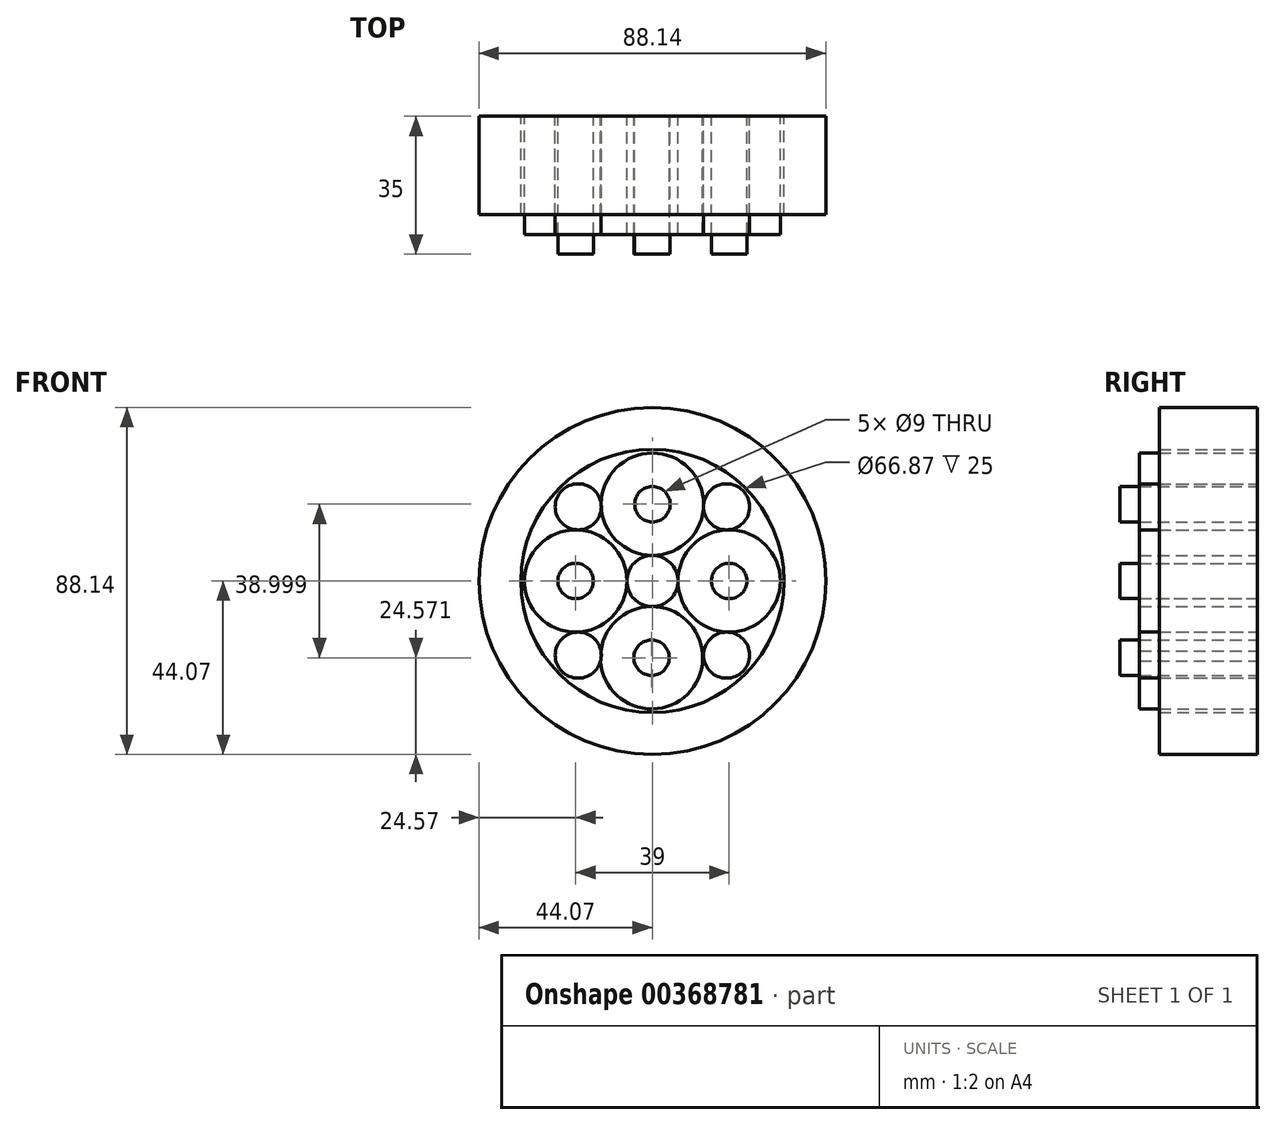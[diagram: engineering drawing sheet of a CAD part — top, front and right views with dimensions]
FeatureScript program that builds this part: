
annotation { "Feature Type Name" : "Feature", "Feature Type Description" : "" }
export const myFeature = defineFeature(function(context is Context, id is Id, definition is map)
    precondition{}
    {
        {
            var Q0;
            Q0=qCreatedBy(makeId("Front.planeOp"),FACE);
            var sketch = newSketch(context, id + "F0", { "sketchPlane" : qUnion([Q0])});
            skCircle(sketch, "E0", {"center": v(0, 0) * mm, "radius": 6.5 * mm});
            skCircle(sketch, "E1", {"center": v(0, 19.5) * mm, "radius": 13 * mm});
            skCircle(sketch, "E2", {"center": v(19.5, 0) * mm, "radius": 13 * mm});
            skCircle(sketch, "E3", {"center": v(-0.21, -19.5) * mm, "radius": 13 * mm});
            skCircle(sketch, "E4", {"center": v(-19.5, 0) * mm, "radius": 13 * mm});
            skCircle(sketch, "E5", {"center": v(0, 0) * mm, "radius": 32.5 * mm});
            skCircle(sketch, "E6", {"center": v(0, 19.5) * mm, "radius": 4.5 * mm});
            skCircle(sketch, "E7", {"center": v(19.5, 0) * mm, "radius": 4.5 * mm});
            skCircle(sketch, "E8", {"center": v(-19.5, 0) * mm, "radius": 4.5 * mm});
            skCircle(sketch, "E9", {"center": v(-0.21, -19.5) * mm, "radius": 4.5 * mm});
            skCircle(sketch, "E10", {"center": v(-18.84, 18.84) * mm, "radius": 5.85 * mm});
            skPoint(sketch, "E10.first.point", {"position": v(-19.05, 13) * mm});
            skPoint(sketch, "E10.second.point", {"position": v(-22.98, 22.98) * mm});
            skPoint(sketch, "E10.third.point", {"position": v(-13, 19.05) * mm});
            skPoint(sketch, "E11.first.point", {"position": v(19.05, 13) * mm});
            skPoint(sketch, "E11.second.point", {"position": v(13, 19.05) * mm});
            skPoint(sketch, "E11.third.point", {"position": v(22.98, 22.98) * mm});
            skCircle(sketch, "E12.1.0", {"center": v(-18.84, -18.84) * mm, "radius": 5.85 * mm});
            skCircle(sketch, "E12.2.0", {"center": v(18.84, -18.84) * mm, "radius": 5.85 * mm});
            skCircle(sketch, "E12.3.0", {"center": v(18.84, 18.84) * mm, "radius": 5.85 * mm});
            skSolve(sketch);
        }
        {
            var Q0;
            Q0=makeQuery(id+"F0.imprint","IMPRINT",FACE,{"disambiguationData":[TD([[makeQuery(id+"F0.imprint","IMPRINT",EDGE,{"derivedFrom":sQuery(id+"F0.wireOp",EDGE,"E6")}),1.0]])]});
            extrude(context, id + "F1", {"entities" : qUnion([Q0]), "depth" : 35 * mm});
        }
        {
            var Q0;
            Q0=makeQuery(id+"F0.imprint","IMPRINT",FACE,{"disambiguationData":[TD([[makeQuery(id+"F0.imprint","IMPRINT",EDGE,{"derivedFrom":sQuery(id+"F0.wireOp",EDGE,"E6")}),-1.0]])]});
            extrude(context, id + "F2", {"entities" : qUnion([Q0]), "depth" : 30 * mm});
        }
        {
            var Q0;
            Q0=makeQuery(id+"F0.imprint","IMPRINT",FACE,{"disambiguationData":[TD([[makeQuery(id+"F0.imprint","IMPRINT",EDGE,{"derivedFrom":sQuery(id+"F0.wireOp",EDGE,"E8")}),-1.0]])]});
            extrude(context, id + "F3", {"entities" : qUnion([Q0]), "depth" : 30 * mm});
        }
        {
            var Q0;
            Q0=makeQuery(id+"F0.imprint","IMPRINT",FACE,{"disambiguationData":[TD([[makeQuery(id+"F0.imprint","IMPRINT",EDGE,{"derivedFrom":sQuery(id+"F0.wireOp",EDGE,"E8")}),1.0]])]});
            extrude(context, id + "F4", {"entities" : qUnion([Q0]), "depth" : 35 * mm});
        }
        {
            var Q0;
            Q0=makeQuery(id+"F0.imprint","IMPRINT",FACE,{"disambiguationData":[TD([[makeQuery(id+"F0.imprint","IMPRINT",EDGE,{"derivedFrom":sQuery(id+"F0.wireOp",EDGE,"E7")}),-1.0]])]});
            extrude(context, id + "F5", {"entities" : qUnion([Q0]), "depth" : 30 * mm});
        }
        {
            var Q0;
            Q0=makeQuery(id+"FklGXc4gm90GgBo_5.opExtrude","CAP_FACE",FACE,{"disambiguationData":[OSD([sQuery(id+"F0.wireOp",EDGE,"E7")])],"isStart":false});
            var Q1;
            Q1=makeQuery(id+"F0.imprint","IMPRINT",FACE,{"disambiguationData":[TD([[makeQuery(id+"F0.imprint","IMPRINT",EDGE,{"derivedFrom":sQuery(id+"F0.wireOp",EDGE,"E9")}),-1.0]])]});
            extrude(context, id + "F6", {"entities" : qUnion([Q0, Q1]), "operationType" : NewBodyOperationType.ADD, "depth" : 30 * mm});
        }
        {
            var Q0;
            Q0=makeQuery(id+"F0.imprint","IMPRINT",FACE,{"disambiguationData":[TD([[makeQuery(id+"F0.imprint","IMPRINT",EDGE,{"derivedFrom":sQuery(id+"F0.wireOp",EDGE,"E7")}),1.0]])]});
            extrude(context, id + "F7", {"entities" : qUnion([Q0]), "depth" : 35 * mm});
        }
        {
            var Q0;
            Q0=makeQuery(id+"F0.imprint","IMPRINT",FACE,{"disambiguationData":[TD([[makeQuery(id+"F0.imprint","IMPRINT",EDGE,{"derivedFrom":sQuery(id+"F0.wireOp",EDGE,"E9")}),-1.0]])]});
            extrude(context, id + "F8", {"entities" : qUnion([Q0]), "depth" : 30 * mm});
        }
        {
            var Q0;
            Q0=makeQuery(id+"F0.imprint","IMPRINT",FACE,{"disambiguationData":[TD([[makeQuery(id+"F0.imprint","IMPRINT",EDGE,{"derivedFrom":sQuery(id+"F0.wireOp",EDGE,"E9")}),1.0]])]});
            extrude(context, id + "F9", {"entities" : qUnion([Q0]), "depth" : 35 * mm});
        }
        {
            var Q0;
            Q0=qCreatedBy(makeId("Front.planeOp"),FACE);
            var sketch = newSketch(context, id + "F10", { "sketchPlane" : qUnion([Q0])});
            skCircle(sketch, "E13", {"center": v(0, 0) * mm, "radius": 33.44 * mm});
            skCircle(sketch, "E14", {"center": v(0, 0) * mm, "radius": 44.07 * mm});
            skSolve(sketch);
        }
        {
            var Q0;
            Q0=makeQuery(id+"F10.imprint","IMPRINT",FACE,{"disambiguationData":[TD([[makeQuery(id+"F10.imprint","IMPRINT",EDGE,{"derivedFrom":sQuery(id+"F10.wireOp",EDGE,"E13")}),-1.0]])]});
            extrude(context, id + "F11", {"entities" : qUnion([Q0]), "depth" : 25 * mm});
        }
        {
            var Q0;
            {var subQ0=sQuery(id+"F0.wireOp",EDGE,"E10");var subQ1=makeQuery(id+"F0.imprint","INTERSECT",VERTEX,{"derivedFrom":[sQuery(id+"F0.wireOp",EDGE,"E5"),subQ0]});Q0=makeQuery(id+"F0.imprint","IMPRINT",FACE,{"disambiguationData":[TD([[makeQuery(id+"F0.imprint","IMPRINT",EDGE,{"disambiguationData":[TD([[subQ1,1.0]])],"derivedFrom":subQ0}),1.0]])]});}
            extrude(context, id + "F12", {"entities" : qUnion([Q0]), "depth" : 30 * mm});
        }
        {
            var Q0;
            Q0=makeQuery(id+"F12.opExtrude","SWEPT_BODY",BODY,{"disambiguationData":[OSD([sQuery(id+"F0.wireOp",EDGE,"E10")])]});
            var Q1;
            Q1=sQuery(id+"F0.wireOp",EDGE,"E0");
            circularPattern(context, id + "F13", {"entities" : qUnion([Q0]), "axis" : qUnion([Q1]), "angle" : 360 * degree, "instanceCount" : 4, "equalSpace" : true});
        }
        {
            var Q0;
            {var subQ0=sQuery(id+"F0.wireOp",EDGE,"E0");var subQ1=makeQuery(id+"F0.imprint","INTERSECT",VERTEX,{"derivedFrom":[subQ0,sQuery(id+"F0.wireOp",EDGE,"E1")]});Q0=makeQuery(id+"F0.imprint","IMPRINT",FACE,{"disambiguationData":[TD([[makeQuery(id+"F0.imprint","IMPRINT",EDGE,{"disambiguationData":[TD([[subQ1,1.0]])],"derivedFrom":subQ0}),1.0]])]});}
            extrude(context, id + "F14", {"entities" : qUnion([Q0]), "depth" : 30 * mm});
        }
    });
